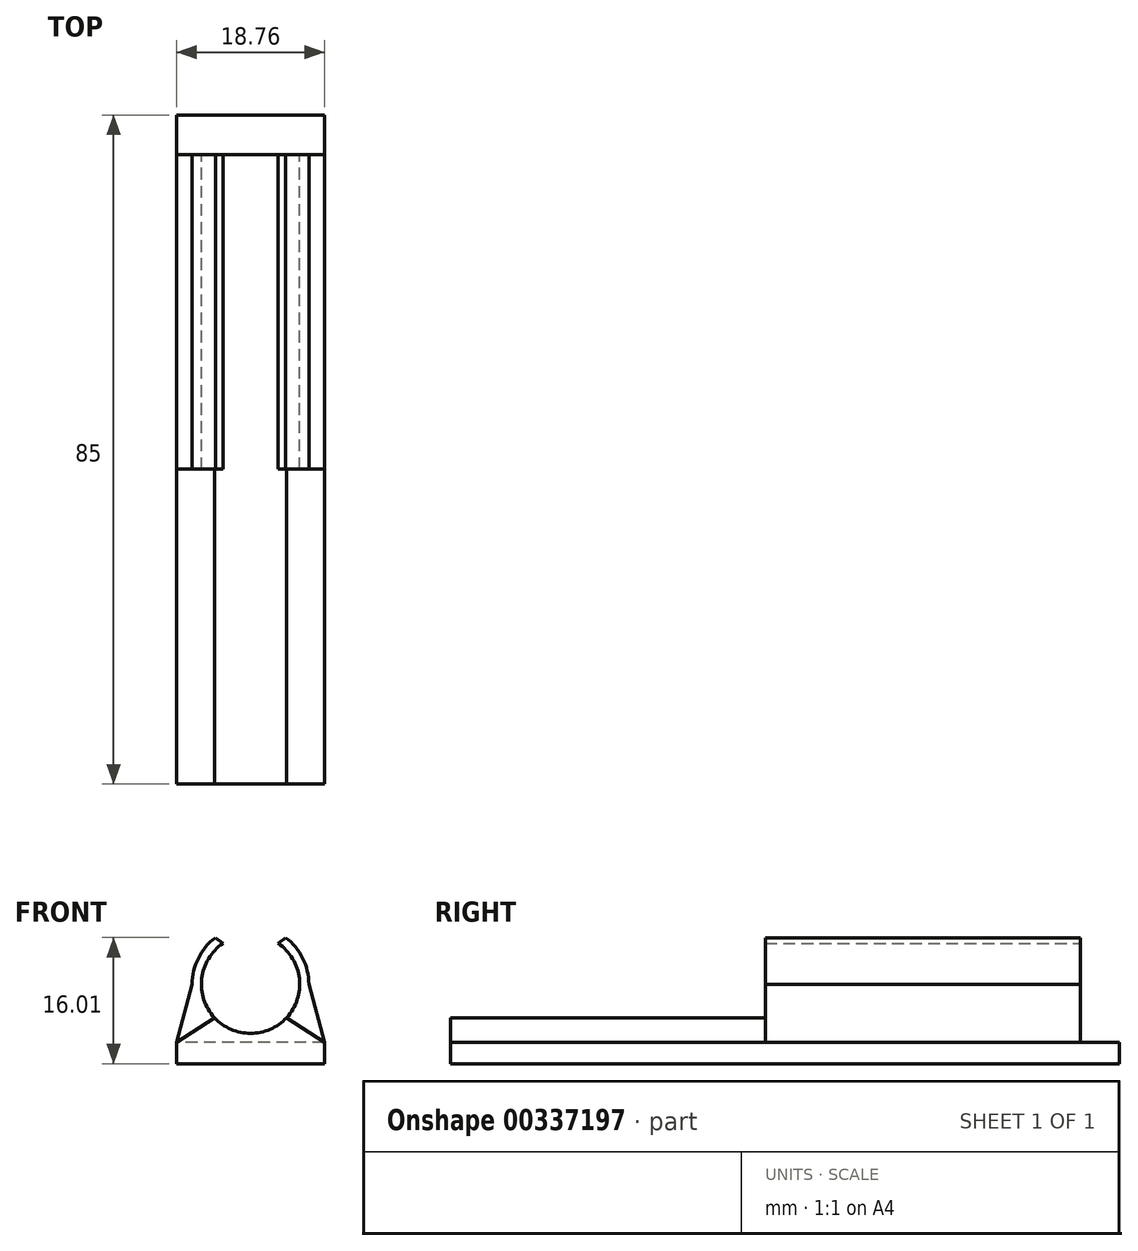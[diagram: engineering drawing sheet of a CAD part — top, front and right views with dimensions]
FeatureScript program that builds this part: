
annotation { "Feature Type Name" : "Feature", "Feature Type Description" : "" }
export const myFeature = defineFeature(function(context is Context, id is Id, definition is map)
    precondition{}
    {
        {
            var Q0;
            Q0=qCreatedBy(makeId("Front.planeOp"),FACE);
            var sketch = newSketch(context, id + "F0", { "sketchPlane" : qUnion([Q0])});
            skArc(sketch, "E0", {"start": v(-3.5, 5.18) * mm, "mid": v(0, -6.25) * mm, "end": v(3.5, 5.18) * mm});
            skPoint(sketch, "E1", {"position": v(3.5, 5.18) * mm});
            skPoint(sketch, "E2.MirrorP", {"position": v(-3.5, 5.18) * mm});
            skArc(sketch, "E3", {"start": v(-4.47, 5.9) * mm, "mid": v(0, -7.4) * mm, "end": v(4.47, 5.9) * mm});
            skPoint(sketch, "E4", {"position": v(-4.47, 5.9) * mm});
            skPoint(sketch, "E5.MirrorP", {"position": v(4.47, 5.9) * mm});
            skLineSegment(sketch, "E6", {"start": v(-4.47, 5.9) * mm, "end": v(-3.5, 5.18) * mm});
            skLineSegment(sketch, "E7.MirrorCS", {"start": v(4.47, 5.9) * mm, "end": v(3.5, 5.18) * mm});
            skLineSegment(sketch, "E8.bottom", {"start": v(0, -7.4) * mm, "end": v(-9.38, -7.4) * mm});
            skLineSegment(sketch, "E8.top", {"start": v(0, -10.1) * mm, "end": v(-9.38, -10.1) * mm});
            skLineSegment(sketch, "E8.left", {"start": v(0, -7.4) * mm, "end": v(0, -10.1) * mm});
            skLineSegment(sketch, "E8.right", {"start": v(-9.38, -7.4) * mm, "end": v(-9.38, -10.1) * mm});
            skLineSegment(sketch, "E9.MirrorCS", {"start": v(0, -7.4) * mm, "end": v(9.38, -7.4) * mm});
            skLineSegment(sketch, "E10.MirrorCS", {"start": v(0, -10.1) * mm, "end": v(9.38, -10.1) * mm});
            skLineSegment(sketch, "E11.MirrorCS", {"start": v(9.38, -7.4) * mm, "end": v(9.38, -10.1) * mm});
            skLineSegment(sketch, "E12", {"start": v(-7.4, 0) * mm, "end": v(-9.38, -7.4) * mm});
            skLineSegment(sketch, "E13.MirrorCS", {"start": v(7.4, 0) * mm, "end": v(9.38, -7.4) * mm});
            skLineSegment(sketch, "E14", {"start": v(4.58, -4.26) * mm, "end": v(9.38, -7.4) * mm});
            skLineSegment(sketch, "E15.MirrorCS", {"start": v(-4.58, -4.26) * mm, "end": v(-9.38, -7.4) * mm});
            skSolve(sketch);
        }
        {
            var Q0;
            {var subQ0=sQuery(id+"F0.wireOp",EDGE,"E14");var subQ1=sQuery(id+"F0.wireOp",EDGE,"E0");var subQ2=makeQuery(id+"F0.imprint","INTERSECT",VERTEX,{"derivedFrom":[subQ1,subQ0]});Q0=makeQuery(id+"F0.imprint","IMPRINT",FACE,{"disambiguationData":[TD([[makeQuery(id+"F0.imprint","IMPRINT",EDGE,{"disambiguationData":[TD([[subQ2,1.0]])],"derivedFrom":subQ1}),-1.0]])]});}
            var Q1;
            {var subQ0=sQuery(id+"F0.wireOp",EDGE,"E9.MirrorCS");Q1=makeQuery(id+"F0.imprint","IMPRINT",FACE,{"disambiguationData":[TD([[makeQuery(id+"F0.imprint","IMPRINT",EDGE,{"derivedFrom":subQ0}),1.0]])]});}
            var Q2;
            {var subQ0=sQuery(id+"F0.wireOp",EDGE,"E8.bottom");Q2=makeQuery(id+"F0.imprint","IMPRINT",FACE,{"disambiguationData":[TD([[makeQuery(id+"F0.imprint","IMPRINT",EDGE,{"derivedFrom":subQ0}),-1.0]])]});}
            var Q3;
            Q3=makeQuery(id+"F0.imprint","IMPRINT",FACE,{"disambiguationData":[TD([[makeQuery(id+"F0.imprint","IMPRINT",EDGE,{"derivedFrom":sQuery(id+"F0.wireOp",EDGE,"E8.bottom")}),1.0]])]});
            var Q4;
            Q4=makeQuery(id+"F0.imprint","IMPRINT",FACE,{"disambiguationData":[TD([[makeQuery(id+"F0.imprint","IMPRINT",EDGE,{"derivedFrom":sQuery(id+"F0.wireOp",EDGE,"E8.left")}),1.0]])]});
            extrude(context, id + "F1", {"entities" : qUnion([Q0, Q1, Q2, Q3, Q4]), "depth" : 80 * mm});
        }
        {
            var Q0;
            {var subQ0=sQuery(id+"F0.wireOp",EDGE,"E12");Q0=makeQuery(id+"F0.imprint","IMPRINT",FACE,{"disambiguationData":[TD([[makeQuery(id+"F0.imprint","IMPRINT",EDGE,{"derivedFrom":subQ0}),1.0]])]});}
            var Q1;
            {var subQ0=sQuery(id+"F0.wireOp",EDGE,"E6");Q1=makeQuery(id+"F0.imprint","IMPRINT",FACE,{"disambiguationData":[TD([[makeQuery(id+"F0.imprint","IMPRINT",EDGE,{"derivedFrom":subQ0}),-1.0]])]});}
            var Q2;
            {var subQ0=sQuery(id+"F0.wireOp",EDGE,"E7.MirrorCS");Q2=makeQuery(id+"F0.imprint","IMPRINT",FACE,{"disambiguationData":[TD([[makeQuery(id+"F0.imprint","IMPRINT",EDGE,{"derivedFrom":subQ0}),1.0]])]});}
            var Q3;
            {var subQ0=sQuery(id+"F0.wireOp",EDGE,"E13.MirrorCS");Q3=makeQuery(id+"F0.imprint","IMPRINT",FACE,{"disambiguationData":[TD([[makeQuery(id+"F0.imprint","IMPRINT",EDGE,{"derivedFrom":subQ0}),-1.0]])]});}
            extrude(context, id + "F2", {"entities" : qUnion([Q0, Q1, Q2, Q3]), "operationType" : NewBodyOperationType.ADD, "depth" : 40 * mm});
        }
        {
            var Q0;
            {var subQ0=sQuery(id+"F0.wireOp",EDGE,"E14");var subQ1=sQuery(id+"F0.wireOp",EDGE,"E3");var subQ2=sQuery(id+"F0.wireOp",EDGE,"E0");var subQ3=sQuery(id+"F0.wireOp",EDGE,"E15.MirrorCS");Q0=makeQuery(id+"F2.boolean.opBoolean","MERGE",FACE,{"derivedFrom":[makeQuery(id+"F1.opExtrude","CAP_FACE",FACE,{"disambiguationData":[OSD([subQ2,sQuery(id+"F0.wireOp",EDGE,"E8.top"),sQuery(id+"F0.wireOp",EDGE,"E8.right"),sQuery(id+"F0.wireOp",EDGE,"E10.MirrorCS"),sQuery(id+"F0.wireOp",EDGE,"E11.MirrorCS"),subQ0,subQ3])],"isStart":true}),makeQuery(id+"F2.opExtrude","CAP_FACE",FACE,{"disambiguationData":[OSD([subQ2,subQ1,sQuery(id+"F0.wireOp",EDGE,"E6"),sQuery(id+"F0.wireOp",EDGE,"E12"),subQ3])],"isStart":true}),makeQuery(id+"F2.opExtrude","CAP_FACE",FACE,{"disambiguationData":[OSD([subQ2,subQ1,sQuery(id+"F0.wireOp",EDGE,"E7.MirrorCS"),sQuery(id+"F0.wireOp",EDGE,"E13.MirrorCS"),subQ0])],"isStart":true})]});}
            var sketch = newSketch(context, id + "F3", { "sketchPlane" : qUnion([Q0])});
            skLineSegment(sketch, "E16.bottom", {"start": v(-9.38, -10.1) * mm, "end": v(9.38, -10.1) * mm});
            skLineSegment(sketch, "E16.top", {"start": v(-9.38, -7.4) * mm, "end": v(9.38, -7.4) * mm});
            skLineSegment(sketch, "E16.left", {"start": v(-9.38, -10.1) * mm, "end": v(-9.38, -7.4) * mm});
            skLineSegment(sketch, "E16.right", {"start": v(9.38, -10.1) * mm, "end": v(9.38, -7.4) * mm});
            skSolve(sketch);
        }
        {
            var Q0;
            Q0=makeQuery(id+"F3.imprint","IMPRINT",FACE,{"disambiguationData":[TD([[makeQuery(id+"F3.imprint","IMPRINT",EDGE,{"derivedFrom":sQuery(id+"F3.wireOp",EDGE,"E16.bottom")}),1.0]])]});
            extrude(context, id + "F4", {"entities" : qUnion([Q0]), "operationType" : NewBodyOperationType.ADD, "depth" : 5 * mm});
        }
    });
